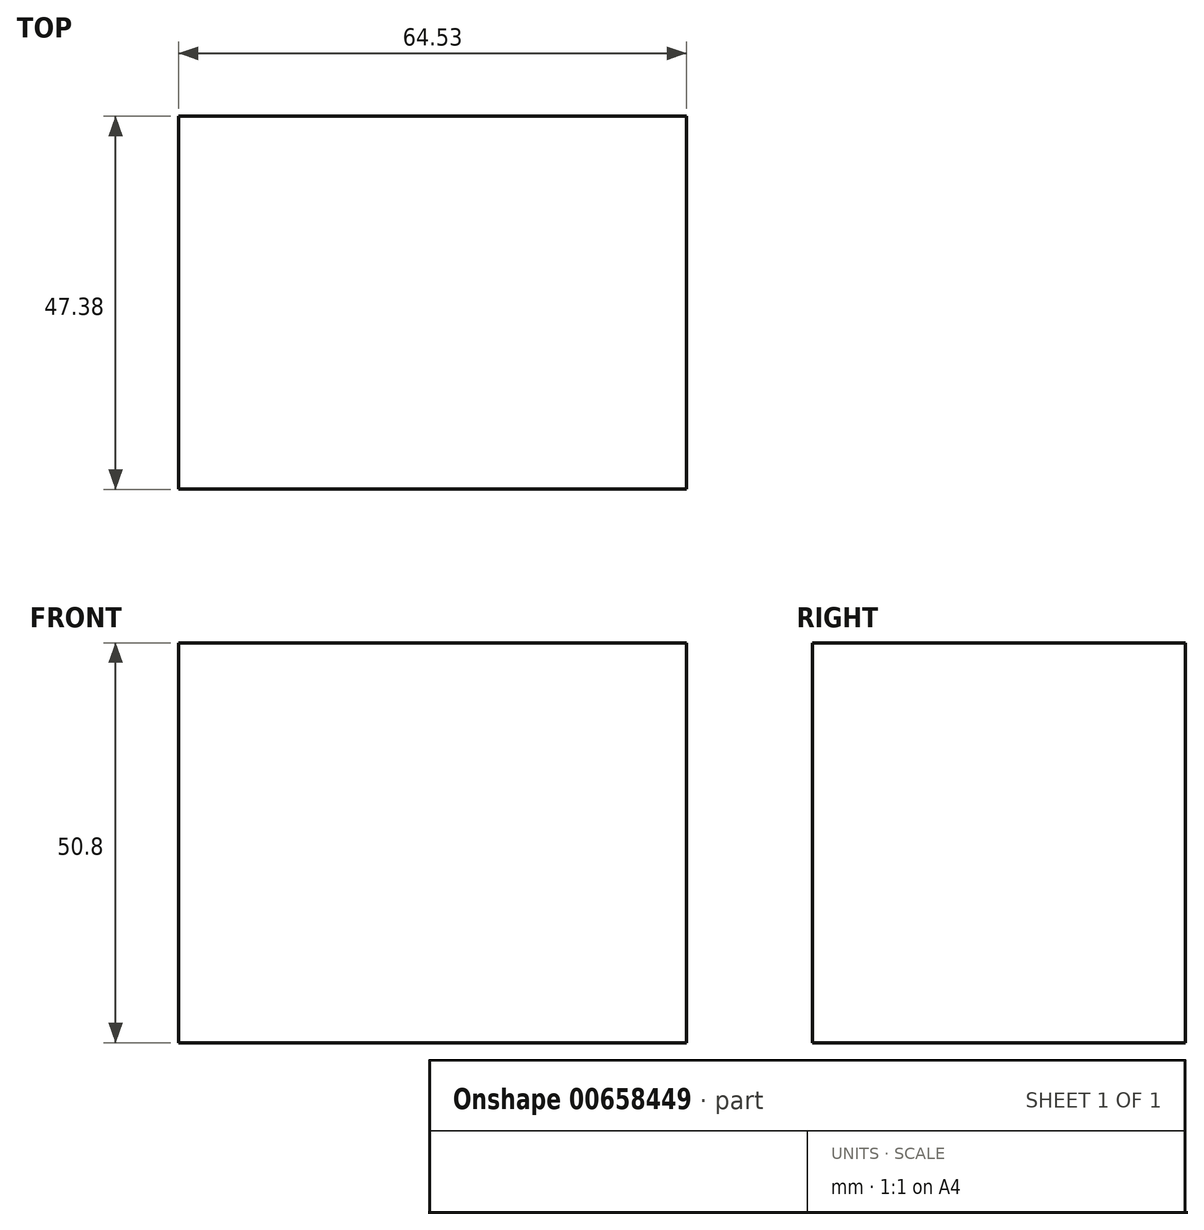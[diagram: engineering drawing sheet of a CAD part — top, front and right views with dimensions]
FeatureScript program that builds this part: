
annotation { "Feature Type Name" : "Feature", "Feature Type Description" : "" }
export const myFeature = defineFeature(function(context is Context, id is Id, definition is map)
    precondition{}
    {
        {
            var Q0;
            Q0=qCreatedBy(makeId("Top.planeOp"),FACE);
            var sketch = newSketch(context, id + "F0", { "sketchPlane" : qUnion([Q0])});
            skLineSegment(sketch, "E0.bottom", {"start": v(-31.25, -19.27) * mm, "end": v(33.28, -19.27) * mm});
            skLineSegment(sketch, "E0.top", {"start": v(-31.25, 28.11) * mm, "end": v(33.28, 28.11) * mm});
            skLineSegment(sketch, "E0.left", {"start": v(-31.25, -19.27) * mm, "end": v(-31.25, 28.11) * mm});
            skLineSegment(sketch, "E0.right", {"start": v(33.28, -19.27) * mm, "end": v(33.28, 28.11) * mm});
            skSolve(sketch);
        }
        {
            var Q0;
            Q0=makeQuery(id+"F0.imprint","IMPRINT",FACE,{"disambiguationData":[TD([[makeQuery(id+"F0.imprint","IMPRINT",EDGE,{"derivedFrom":sQuery(id+"F0.wireOp",EDGE,"E0.bottom")}),1.0]])]});
            extrude(context, id + "F1", {"entities" : qUnion([Q0]), "depth" : 50.8 * mm, "offsetDistance" : 25.4 * mm});
        }
    });
